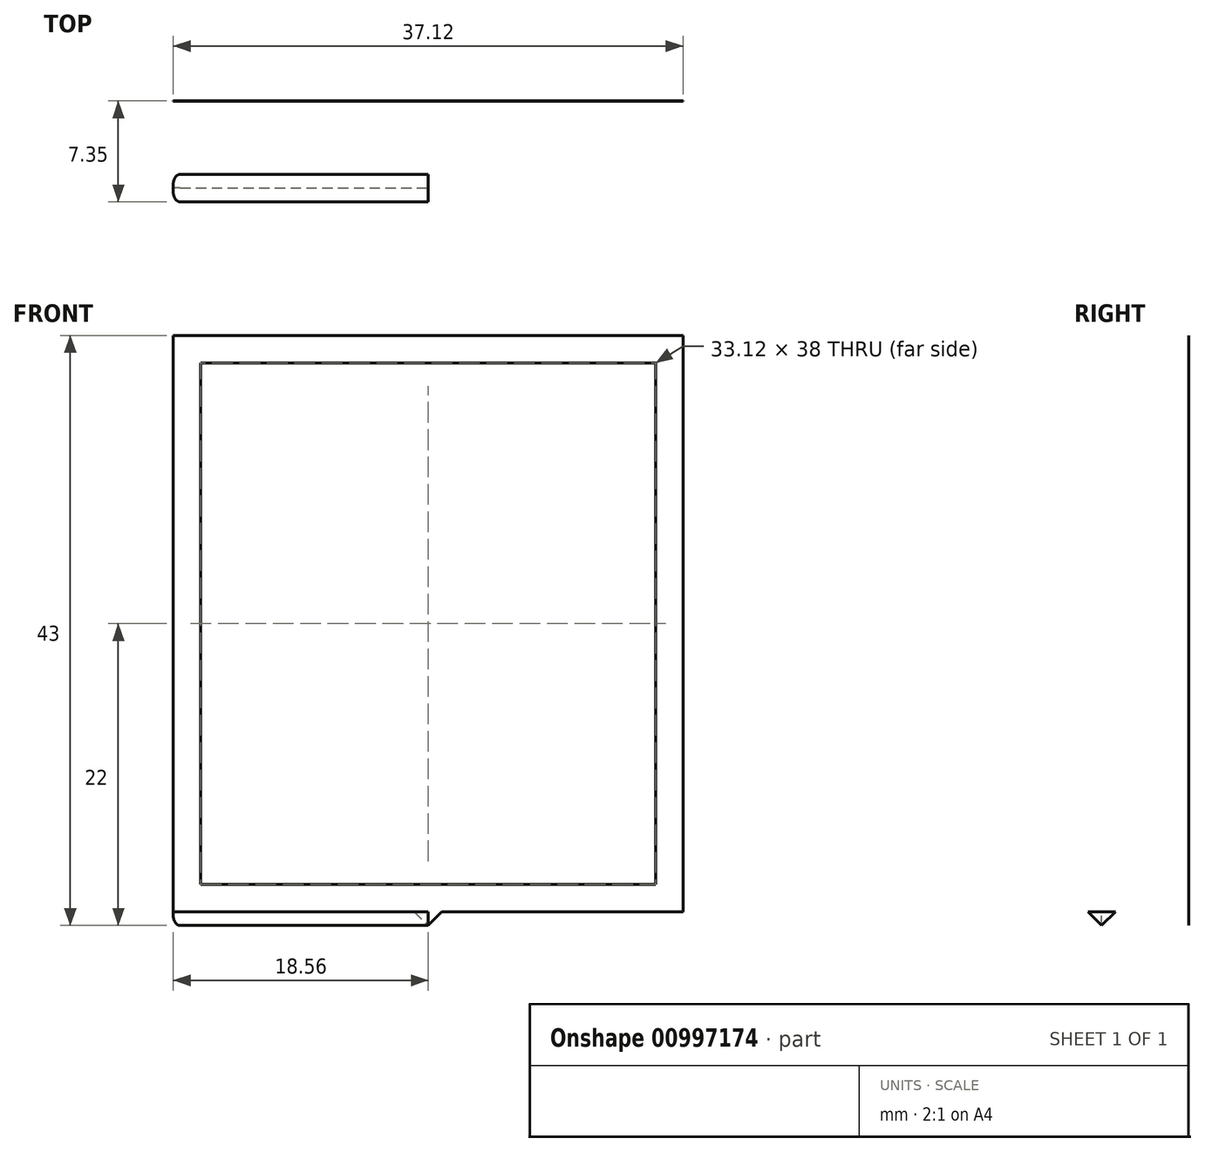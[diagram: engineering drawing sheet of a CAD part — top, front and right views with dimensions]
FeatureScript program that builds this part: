
annotation { "Feature Type Name" : "Feature", "Feature Type Description" : "" }
export const myFeature = defineFeature(function(context is Context, id is Id, definition is map)
    precondition{}
    {
        {
            var Q0;
            Q0=qCreatedBy(makeId("Front.planeOp"),FACE);
            var sketch = newSketch(context, id + "F0", { "sketchPlane" : qUnion([Q0])});
            skLineSegment(sketch, "E0", {"start": v(-24.91, 16.4) * mm, "end": v(-18.56, 16.4) * mm});
            skLineSegment(sketch, "E1", {"start": v(-18.56, 16.4) * mm, "end": v(-18.56, 0) * mm});
            skLineSegment(sketch, "E2", {"start": v(-18.56, 0) * mm, "end": v(0, 0) * mm});
            skLineSegment(sketch, "E3", {"start": v(0, 0) * mm, "end": v(0, 2) * mm});
            skLineSegment(sketch, "E4", {"start": v(0, 2) * mm, "end": v(-16.56, 2) * mm});
            skLineSegment(sketch, "E5", {"start": v(-16.56, 2) * mm, "end": v(-16.56, 40) * mm});
            skLineSegment(sketch, "E6", {"start": v(-16.56, 40) * mm, "end": v(0, 40) * mm});
            skLineSegment(sketch, "E7", {"start": v(0, 40) * mm, "end": v(0, 42) * mm});
            skLineSegment(sketch, "E8", {"start": v(0, 42) * mm, "end": v(-18.56, 42) * mm});
            skLineSegment(sketch, "E9", {"start": v(-18.56, 42) * mm, "end": v(-18.56, 18.4) * mm});
            skLineSegment(sketch, "E10", {"start": v(-18.56, 18.4) * mm, "end": v(-24.91, 18.4) * mm});
            skLineSegment(sketch, "E11", {"start": v(-24.91, 18.4) * mm, "end": v(-24.91, 16.4) * mm});
            skLineSegment(sketch, "E12", {"start": v(-16.56, 2) * mm, "end": v(-18.56, 2) * mm, "construction": true});
            skSolve(sketch);
        }
        {
            var Q0;
            Q0=qSketchRegion(id+"F0",true);
            extrude(context, id + "F1", {"entities" : qUnion([Q0]), "depth" : 1 / 50.8 * mm, "offsetDistance" : 25 * mm});
        }
        {
            var Q0;
            Q0=qCreatedBy(makeId("Front.planeOp"),FACE);
            var sketch = newSketch(context, id + "F2", { "sketchPlane" : qUnion([Q0])});
            skPoint(sketch, "E13.0", {"position": v(-18.56, 18.4) * mm});
            skPoint(sketch, "E14.0", {"position": v(-24.91, 16.4) * mm});
            skLineSegment(sketch, "E15.bottom", {"start": v(-24.91, 16.4) * mm, "end": v(-18.56, 16.4) * mm});
            skLineSegment(sketch, "E15.top", {"start": v(-24.91, 18.4) * mm, "end": v(-18.56, 18.4) * mm});
            skLineSegment(sketch, "E15.left", {"start": v(-24.91, 16.4) * mm, "end": v(-24.91, 18.4) * mm});
            skLineSegment(sketch, "E15.right", {"start": v(-18.56, 16.4) * mm, "end": v(-18.56, 18.4) * mm});
            skSolve(sketch);
        }
        {
            var Q0;
            Q0=qSketchRegion(id+"F2",true);
            extrude(context, id + "F3", {"entities" : qUnion([Q0]), "operationType" : NewBodyOperationType.REMOVE, "depth" : 25 * mm, "offsetDistance" : 25 * mm});
        }
        {
            var Q0;
            Q0=makeQuery(id+"FlJoKYSt8OexyGq_1.boolean.opBoolean","MERGE",FACE,{"derivedFrom":[makeQuery(id+"F1.opExtrude","SWEPT_FACE",FACE,{"disambiguationData":[OSD([sQuery(id+"F0.wireOp",EDGE,"E3")])]}),makeQuery(id+"FlJoKYSt8OexyGq_1.opExtrude","SWEPT_FACE",FACE,{"disambiguationData":[OSD([sQuery(id+"FTgjrMQJr4GTSXr_1.wireOp",EDGE,"iIzk7QKK-2KnJ-uT3C-CxSF-DB9qCKoUd3UN.right")])]})]});
            var sketch = newSketch(context, id + "F4", { "sketchPlane" : qUnion([Q0])});
            skPoint(sketch, "E16", {"position": v(-6.35, 2) * mm});
            skLineSegment(sketch, "E17", {"start": v(-6.35, 0) * mm, "end": v(-6.35, -1) * mm, "construction": true});
            skArc(sketch, "E18", {"start": v(-7.35, 0) * mm, "mid": v(-6.35, -1) * mm, "end": v(-5.35, 0) * mm, "construction": true});
            skLineSegment(sketch, "E19", {"start": v(-5.35, 0) * mm, "end": v(-7.35, 0) * mm});
            skLineSegment(sketch, "E20", {"start": v(-5.35, 0) * mm, "end": v(-6.35, -1) * mm});
            skLineSegment(sketch, "E21", {"start": v(-7.35, 0) * mm, "end": v(-6.35, -1) * mm});
            skSolve(sketch);
        }
        {
            var Q0;
            Q0=qSketchRegion(id+"F4",true);
            var Q1;
            Q1=makeQuery(id+"F1.opExtrude","CAP_VERTEX",VERTEX,{"disambiguationData":[OSD([sQuery(id+"F0.wireOp",EDGE,"E1"),sQuery(id+"F0.wireOp",EDGE,"E2")])],"isStart":true});
            extrude(context, id + "F5", {"entities" : qUnion([Q0]), "operationType" : NewBodyOperationType.ADD, "endBound" : BoundingType.UP_TO_VERTEX, "oppositeDirection" : true, "depth" : 25 * mm, "endBoundEntityVertex" : qUnion([Q1]), "offsetDistance" : 25 * mm});
        }
        {
            var Q0;
            Q0=makeQuery(id+"F1.opExtrude","SWEPT_BODY",BODY,{"disambiguationData":[OSD([sQuery(id+"F0.wireOp",EDGE,"E0"),sQuery(id+"F0.wireOp",EDGE,"E1"),sQuery(id+"F0.wireOp",EDGE,"E2"),sQuery(id+"F0.wireOp",EDGE,"E3"),sQuery(id+"F0.wireOp",EDGE,"E4"),sQuery(id+"F0.wireOp",EDGE,"E5"),sQuery(id+"F0.wireOp",EDGE,"E6"),sQuery(id+"F0.wireOp",EDGE,"E7"),sQuery(id+"F0.wireOp",EDGE,"E8"),sQuery(id+"F0.wireOp",EDGE,"E9"),sQuery(id+"F0.wireOp",EDGE,"E10"),sQuery(id+"F0.wireOp",EDGE,"E11")])]});
            var Q1;
            Q1=qCreatedBy(makeId("Right.planeOp"),FACE);
            mirror(context, id + "F6", {"operationType" : NewBodyOperationType.ADD, "entities" : qUnion([Q0]), "mirrorPlane" : qUnion([Q1])});
        }
        {
            var Q0;
            {var subQ0=makeQuery(id+"F1.opExtrude","SWEPT_FACE",FACE,{"disambiguationData":[OSD([sQuery(id+"F0.wireOp",EDGE,"E8")])]});Q0=makeQuery(id+"F6.boolean.opBoolean","MERGE",FACE,{"derivedFrom":[subQ0,makeQuery(id+"F6.opPattern","COPY",FACE,{"derivedFrom":subQ0,"instanceName":"1"})]});}
            var sketch = newSketch(context, id + "F7", { "sketchPlane" : qUnion([Q0])});
            skPoint(sketch, "E22", {"position": v(-11.56, -6.35) * mm});
            skPoint(sketch, "E22.positionSnap0", {"position": v(-18.56, -6.35) * mm});
            skPoint(sketch, "E23", {"position": v(0, -6.35) * mm});
            skPoint(sketch, "E24", {"position": v(11.56, -6.35) * mm});
            skLineSegment(sketch, "E25", {"start": v(11.56, -6.35) * mm, "end": v(0, -6.35) * mm, "construction": true});
            skLineSegment(sketch, "E26", {"start": v(0, -6.35) * mm, "end": v(-11.56, -6.35) * mm, "construction": true});
            skSolve(sketch);
        }
        {
            var Q0;
            {var subQ0=makeQuery(id+"F1.opExtrude","CAP_FACE",FACE,{"disambiguationData":[OSD([sQuery(id+"F0.wireOp",EDGE,"E0"),sQuery(id+"F0.wireOp",EDGE,"E1"),sQuery(id+"F0.wireOp",EDGE,"E2"),sQuery(id+"F0.wireOp",EDGE,"E3"),sQuery(id+"F0.wireOp",EDGE,"E4"),sQuery(id+"F0.wireOp",EDGE,"E5"),sQuery(id+"F0.wireOp",EDGE,"E6"),sQuery(id+"F0.wireOp",EDGE,"E7"),sQuery(id+"F0.wireOp",EDGE,"E8"),sQuery(id+"F0.wireOp",EDGE,"E9"),sQuery(id+"F0.wireOp",EDGE,"E10"),sQuery(id+"F0.wireOp",EDGE,"E11")])],"isStart":true});Q0=makeQuery(id+"F6.boolean.opBoolean","MERGE",FACE,{"derivedFrom":[subQ0,makeQuery(id+"F6.opPattern","COPY",FACE,{"derivedFrom":subQ0,"instanceName":"1"})]});}
            var sketch = newSketch(context, id + "F8", { "sketchPlane" : qUnion([Q0])});
            skArc(sketch, "E27", {"start": v(-1, 0) * mm, "mid": v(0, -1) * mm, "end": v(1, 0) * mm, "construction": true});
            skLineSegment(sketch, "E28", {"start": v(-1, 0) * mm, "end": v(1, 0) * mm});
            skLineSegment(sketch, "E29", {"start": v(1, 0) * mm, "end": v(0, -1) * mm});
            skLineSegment(sketch, "E30", {"start": v(0, -1) * mm, "end": v(-1, 0) * mm});
            skSolve(sketch);
        }
        {
            var Q0;
            Q0=qSketchRegion(id+"F8",true);
            var Q1;
            {var subQ0=makeQuery(id+"F1.opExtrude","CAP_FACE",FACE,{"disambiguationData":[OSD([sQuery(id+"F0.wireOp",EDGE,"E0"),sQuery(id+"F0.wireOp",EDGE,"E1"),sQuery(id+"F0.wireOp",EDGE,"E2"),sQuery(id+"F0.wireOp",EDGE,"E3"),sQuery(id+"F0.wireOp",EDGE,"E4"),sQuery(id+"F0.wireOp",EDGE,"E5"),sQuery(id+"F0.wireOp",EDGE,"E6"),sQuery(id+"F0.wireOp",EDGE,"E7"),sQuery(id+"F0.wireOp",EDGE,"E8"),sQuery(id+"F0.wireOp",EDGE,"E9"),sQuery(id+"F0.wireOp",EDGE,"E10"),sQuery(id+"F0.wireOp",EDGE,"E11")])],"isStart":false});Q1=makeQuery(id+"F6.boolean.opBoolean","MERGE",FACE,{"derivedFrom":[subQ0,makeQuery(id+"F6.opPattern","COPY",FACE,{"derivedFrom":subQ0,"instanceName":"1"})]});}
            extrude(context, id + "F9", {"entities" : qUnion([Q0]), "operationType" : NewBodyOperationType.ADD, "endBound" : BoundingType.UP_TO_SURFACE, "oppositeDirection" : true, "depth" : 25 * mm, "endBoundEntityFace" : qUnion([Q1]), "offsetDistance" : 25 * mm});
        }
        {
            var Q0;
            Q0=sQuery(id+"F7.wireOp",VERTEX,"E22");
            var Q1;
            Q1=sQuery(id+"F7.wireOp",VERTEX,"E23");
            var Q2;
            Q2=sQuery(id+"F7.wireOp",VERTEX,"E24");
            var Q3;
            Q3=makeQuery(id+"F1.opExtrude","SWEPT_BODY",BODY,{"disambiguationData":[OSD([sQuery(id+"F0.wireOp",EDGE,"E0"),sQuery(id+"F0.wireOp",EDGE,"E1"),sQuery(id+"F0.wireOp",EDGE,"E2"),sQuery(id+"F0.wireOp",EDGE,"E3"),sQuery(id+"F0.wireOp",EDGE,"E4"),sQuery(id+"F0.wireOp",EDGE,"E5"),sQuery(id+"F0.wireOp",EDGE,"E6"),sQuery(id+"F0.wireOp",EDGE,"E7"),sQuery(id+"F0.wireOp",EDGE,"E8"),sQuery(id+"F0.wireOp",EDGE,"E9"),sQuery(id+"F0.wireOp",EDGE,"E10"),sQuery(id+"F0.wireOp",EDGE,"E11")])]});
            hole(context, id + "F10", {"style" : HoleStyle.C_BORE, "endStyle" : HoleEndStyle.THROUGH, "holeDiameter" : 1 * mm, "cBoreDiameter" : 2 * mm, "cBoreDepth" : 41 * mm, "majorDiameter" : 5 * mm, "isTappedThrough" : true, "tappedDepth" : 12 * mm, "tapClearance" : 3, "startFromSketch" : true, "locations" : qUnion([Q0, Q1, Q2]), "scope" : qUnion([Q3])});
        }
        {
            var Q0;
            Q0=makeQuery(id+"F6.opPattern","COPY",EDGE,{"derivedFrom":makeQuery(id+"F3.boolean.opBoolean","INTERSECT",EDGE,{"derivedFrom":[makeQuery(id+"F1.opExtrude","CAP_FACE",FACE,{"disambiguationData":[OSD([sQuery(id+"F0.wireOp",EDGE,"E0"),sQuery(id+"F0.wireOp",EDGE,"E1"),sQuery(id+"F0.wireOp",EDGE,"E2"),sQuery(id+"F0.wireOp",EDGE,"E3"),sQuery(id+"F0.wireOp",EDGE,"E4"),sQuery(id+"F0.wireOp",EDGE,"E5"),sQuery(id+"F0.wireOp",EDGE,"E6"),sQuery(id+"F0.wireOp",EDGE,"E7"),sQuery(id+"F0.wireOp",EDGE,"E8"),sQuery(id+"F0.wireOp",EDGE,"E9"),sQuery(id+"F0.wireOp",EDGE,"E10"),sQuery(id+"F0.wireOp",EDGE,"E11")])],"isStart":false}),makeQuery(id+"F3.opExtrude","SWEPT_FACE",FACE,{"disambiguationData":[OSD([sQuery(id+"F2.wireOp",EDGE,"E15.right")])]})]}),"instanceName":"1"});
            var Q1;
            Q1=makeQuery(id+"F6.opPattern","COPY",EDGE,{"derivedFrom":makeQuery(id+"F1.opExtrude","CAP_EDGE",EDGE,{"disambiguationData":[OSD([sQuery(id+"F0.wireOp",EDGE,"E5")])],"isStart":false}),"instanceName":"1"});
            var Q2;
            {var subQ0=makeQuery(id+"F1.opExtrude","CAP_EDGE",EDGE,{"disambiguationData":[OSD([sQuery(id+"F0.wireOp",EDGE,"E8")])],"isStart":false});Q2=makeQuery(id+"F6.boolean.opBoolean","MERGE",EDGE,{"derivedFrom":[subQ0,makeQuery(id+"F6.opPattern","COPY",EDGE,{"derivedFrom":subQ0,"instanceName":"1"})]});}
            var Q3;
            {var subQ0=makeQuery(id+"F1.opExtrude","CAP_EDGE",EDGE,{"disambiguationData":[OSD([sQuery(id+"F0.wireOp",EDGE,"E6")])],"isStart":false});Q3=makeQuery(id+"F6.boolean.opBoolean","MERGE",EDGE,{"derivedFrom":[subQ0,makeQuery(id+"F6.opPattern","COPY",EDGE,{"derivedFrom":subQ0,"instanceName":"1"})]});}
            var Q4;
            Q4=makeQuery(id+"F1.opExtrude","CAP_EDGE",EDGE,{"disambiguationData":[OSD([sQuery(id+"F0.wireOp",EDGE,"E5")])],"isStart":false});
            var Q5;
            Q5=makeQuery(id+"F3.boolean.opBoolean","INTERSECT",EDGE,{"derivedFrom":[makeQuery(id+"F1.opExtrude","CAP_FACE",FACE,{"disambiguationData":[OSD([sQuery(id+"F0.wireOp",EDGE,"E0"),sQuery(id+"F0.wireOp",EDGE,"E1"),sQuery(id+"F0.wireOp",EDGE,"E2"),sQuery(id+"F0.wireOp",EDGE,"E3"),sQuery(id+"F0.wireOp",EDGE,"E4"),sQuery(id+"F0.wireOp",EDGE,"E5"),sQuery(id+"F0.wireOp",EDGE,"E6"),sQuery(id+"F0.wireOp",EDGE,"E7"),sQuery(id+"F0.wireOp",EDGE,"E8"),sQuery(id+"F0.wireOp",EDGE,"E9"),sQuery(id+"F0.wireOp",EDGE,"E10"),sQuery(id+"F0.wireOp",EDGE,"E11")])],"isStart":false}),makeQuery(id+"F3.opExtrude","SWEPT_FACE",FACE,{"disambiguationData":[OSD([sQuery(id+"F2.wireOp",EDGE,"E15.right")])]})]});
            var Q6;
            Q6=makeQuery(id+"F6.opPattern","COPY",EDGE,{"derivedFrom":makeQuery(id+"F1.opExtrude","SWEPT_EDGE",EDGE,{"disambiguationData":[OSD([sQuery(id+"F0.wireOp",EDGE,"E8"),sQuery(id+"F0.wireOp",EDGE,"E9")])]}),"instanceName":"1"});
            var Q7;
            Q7=makeQuery(id+"F1.opExtrude","SWEPT_EDGE",EDGE,{"disambiguationData":[OSD([sQuery(id+"F0.wireOp",EDGE,"E8"),sQuery(id+"F0.wireOp",EDGE,"E9")])]});
            var Q8;
            Q8=makeQuery(id+"F6.opPattern","COPY",EDGE,{"derivedFrom":makeQuery(id+"F3.boolean.opBoolean","MERGE",EDGE,{"derivedFrom":[makeQuery(id+"F1.opExtrude","CAP_EDGE",EDGE,{"disambiguationData":[OSD([sQuery(id+"F0.wireOp",EDGE,"E1")])],"isStart":true}),makeQuery(id+"F1.opExtrude","CAP_EDGE",EDGE,{"disambiguationData":[OSD([sQuery(id+"F0.wireOp",EDGE,"E9")])],"isStart":true})],"fromTools":[makeQuery(id+"F3.opExtrude","CAP_EDGE",EDGE,{"disambiguationData":[OSD([sQuery(id+"F2.wireOp",EDGE,"E15.right")])],"isStart":true})]}),"instanceName":"1"});
            var Q9;
            {var subQ0=makeQuery(id+"F1.opExtrude","CAP_EDGE",EDGE,{"disambiguationData":[OSD([sQuery(id+"F0.wireOp",EDGE,"E8")])],"isStart":true});Q9=makeQuery(id+"F6.boolean.opBoolean","MERGE",EDGE,{"derivedFrom":[subQ0,makeQuery(id+"F6.opPattern","COPY",EDGE,{"derivedFrom":subQ0,"instanceName":"1"})]});}
            var Q10;
            Q10=makeQuery(id+"F3.boolean.opBoolean","MERGE",EDGE,{"derivedFrom":[makeQuery(id+"F1.opExtrude","CAP_EDGE",EDGE,{"disambiguationData":[OSD([sQuery(id+"F0.wireOp",EDGE,"E1")])],"isStart":true}),makeQuery(id+"F1.opExtrude","CAP_EDGE",EDGE,{"disambiguationData":[OSD([sQuery(id+"F0.wireOp",EDGE,"E9")])],"isStart":true})],"fromTools":[makeQuery(id+"F3.opExtrude","CAP_EDGE",EDGE,{"disambiguationData":[OSD([sQuery(id+"F2.wireOp",EDGE,"E15.right")])],"isStart":true})]});
            var Q11;
            {var subQ0=makeQuery(id+"F1.opExtrude","CAP_EDGE",EDGE,{"disambiguationData":[OSD([sQuery(id+"F0.wireOp",EDGE,"E6")])],"isStart":true});Q11=makeQuery(id+"F6.boolean.opBoolean","MERGE",EDGE,{"derivedFrom":[subQ0,makeQuery(id+"F6.opPattern","COPY",EDGE,{"derivedFrom":subQ0,"instanceName":"1"})]});}
            var Q12;
            Q12=makeQuery(id+"F6.opPattern","COPY",EDGE,{"derivedFrom":makeQuery(id+"F1.opExtrude","CAP_EDGE",EDGE,{"disambiguationData":[OSD([sQuery(id+"F0.wireOp",EDGE,"E5")])],"isStart":true}),"instanceName":"1"});
            var Q13;
            Q13=makeQuery(id+"F1.opExtrude","CAP_EDGE",EDGE,{"disambiguationData":[OSD([sQuery(id+"F0.wireOp",EDGE,"E5")])],"isStart":true});
            var Q14;
            {var subQ0=makeQuery(id+"F1.opExtrude","CAP_EDGE",EDGE,{"disambiguationData":[OSD([sQuery(id+"F0.wireOp",EDGE,"E4")])],"isStart":true});Q14=makeQuery(id+"F6.boolean.opBoolean","MERGE",EDGE,{"derivedFrom":[subQ0,makeQuery(id+"F6.opPattern","COPY",EDGE,{"derivedFrom":subQ0,"instanceName":"1"})]});}
            var Q15;
            {var subQ0=sQuery(id+"F0.wireOp",EDGE,"E2");var subQ2=sQuery(id+"F0.wireOp",EDGE,"E1");var subQ3=makeQuery(id+"F1.opExtrude","SWEPT_FACE",FACE,{"disambiguationData":[OSD([subQ2])]});var subQ13=makeQuery(id+"F1.opExtrude","CAP_EDGE",EDGE,{"disambiguationData":[OSD([subQ0])],"isStart":true});Q15=makeQuery(id+"F9.boolean.opBoolean","SPLIT",EDGE,{"disambiguationData":[TD([subQ3])],"derivedFrom":makeQuery(id+"F6.boolean.opBoolean","MERGE",EDGE,{"derivedFrom":[subQ13,makeQuery(id+"F6.opPattern","COPY",EDGE,{"derivedFrom":subQ13,"instanceName":"1"})]})});}
            var Q16;
            {var subQ0=sQuery(id+"F0.wireOp",EDGE,"E2");var subQ12=sQuery(id+"F8.wireOp",EDGE,"E30");var subQ13=makeQuery(id+"F1.opExtrude","CAP_EDGE",EDGE,{"disambiguationData":[OSD([subQ0])],"isStart":true});Q16=makeQuery(id+"F9.boolean.opBoolean","SPLIT",EDGE,{"disambiguationData":[TD([makeQuery(id+"F9.opExtrude","SWEPT_FACE",FACE,{"disambiguationData":[OSD([subQ12])]})])],"derivedFrom":makeQuery(id+"F6.boolean.opBoolean","MERGE",EDGE,{"derivedFrom":[subQ13,makeQuery(id+"F6.opPattern","COPY",EDGE,{"derivedFrom":subQ13,"instanceName":"1"})]})});}
            var Q17;
            {var subQ2=sQuery(id+"F0.wireOp",EDGE,"E2");var subQ5=sQuery(id+"F0.wireOp",EDGE,"E1");var subQ6=makeQuery(id+"F1.opExtrude","SWEPT_FACE",FACE,{"disambiguationData":[OSD([subQ5])]});var subQ13=makeQuery(id+"F1.opExtrude","CAP_EDGE",EDGE,{"disambiguationData":[OSD([subQ2])],"isStart":false});Q17=makeQuery(id+"F9.boolean.opBoolean","SPLIT",EDGE,{"disambiguationData":[TD([subQ6])],"derivedFrom":makeQuery(id+"F6.boolean.opBoolean","MERGE",EDGE,{"derivedFrom":[subQ13,makeQuery(id+"F6.opPattern","COPY",EDGE,{"derivedFrom":subQ13,"instanceName":"1"})]})});}
            var Q18;
            {var subQ8=sQuery(id+"F0.wireOp",EDGE,"E2");var subQ10=sQuery(id+"F8.wireOp",EDGE,"E30");var subQ13=makeQuery(id+"F1.opExtrude","CAP_EDGE",EDGE,{"disambiguationData":[OSD([subQ8])],"isStart":false});Q18=makeQuery(id+"F9.boolean.opBoolean","SPLIT",EDGE,{"disambiguationData":[TD([makeQuery(id+"F9.opExtrude","SWEPT_FACE",FACE,{"disambiguationData":[OSD([subQ10])]})])],"derivedFrom":makeQuery(id+"F6.boolean.opBoolean","MERGE",EDGE,{"derivedFrom":[subQ13,makeQuery(id+"F6.opPattern","COPY",EDGE,{"derivedFrom":subQ13,"instanceName":"1"})]})});}
            var Q19;
            {var subQ0=makeQuery(id+"F1.opExtrude","CAP_EDGE",EDGE,{"disambiguationData":[OSD([sQuery(id+"F0.wireOp",EDGE,"E4")])],"isStart":false});Q19=makeQuery(id+"F6.boolean.opBoolean","MERGE",EDGE,{"derivedFrom":[subQ0,makeQuery(id+"F6.opPattern","COPY",EDGE,{"derivedFrom":subQ0,"instanceName":"1"})]});}
            var Q20;
            {var subQ1=sQuery(id+"F0.wireOp",EDGE,"E2");var subQ2=sQuery(id+"F0.wireOp",EDGE,"E1");var subQ3=sQuery(id+"F4.wireOp",EDGE,"E21");Q20=makeQuery(id+"F6.opPattern","COPY",EDGE,{"derivedFrom":makeQuery(id+"F5.boolean.opBoolean","SPLIT",EDGE,{"disambiguationData":[TD([makeQuery(id+"F5.opExtrude","SWEPT_FACE",FACE,{"disambiguationData":[OSD([subQ3])]})])],"derivedFrom":makeQuery(id+"F1.opExtrude","SWEPT_EDGE",EDGE,{"disambiguationData":[OSD([subQ2,subQ1])]})}),"instanceName":"1"});}
            var Q21;
            {var subQ0=sQuery(id+"F0.wireOp",EDGE,"E2");var subQ1=sQuery(id+"F0.wireOp",EDGE,"E1");var subQ3=sQuery(id+"F4.wireOp",EDGE,"E20");Q21=makeQuery(id+"F6.opPattern","COPY",EDGE,{"derivedFrom":makeQuery(id+"F5.boolean.opBoolean","SPLIT",EDGE,{"disambiguationData":[TD([makeQuery(id+"F5.opExtrude","SWEPT_FACE",FACE,{"disambiguationData":[OSD([subQ3])]})])],"derivedFrom":makeQuery(id+"F1.opExtrude","SWEPT_EDGE",EDGE,{"disambiguationData":[OSD([subQ1,subQ0])]})}),"instanceName":"1"});}
            var Q22;
            {var subQ1=sQuery(id+"F0.wireOp",EDGE,"E2");var subQ2=sQuery(id+"F0.wireOp",EDGE,"E1");var subQ3=sQuery(id+"F4.wireOp",EDGE,"E21");Q22=makeQuery(id+"F5.boolean.opBoolean","SPLIT",EDGE,{"disambiguationData":[TD([makeQuery(id+"F5.opExtrude","SWEPT_FACE",FACE,{"disambiguationData":[OSD([subQ3])]})])],"derivedFrom":makeQuery(id+"F1.opExtrude","SWEPT_EDGE",EDGE,{"disambiguationData":[OSD([subQ2,subQ1])]})});}
            var Q23;
            {var subQ0=sQuery(id+"F0.wireOp",EDGE,"E2");var subQ1=sQuery(id+"F0.wireOp",EDGE,"E1");var subQ3=sQuery(id+"F4.wireOp",EDGE,"E20");Q23=makeQuery(id+"F5.boolean.opBoolean","SPLIT",EDGE,{"disambiguationData":[TD([makeQuery(id+"F5.opExtrude","SWEPT_FACE",FACE,{"disambiguationData":[OSD([subQ3])]})])],"derivedFrom":makeQuery(id+"F1.opExtrude","SWEPT_EDGE",EDGE,{"disambiguationData":[OSD([subQ1,subQ0])]})});}
            var Q24;
            Q24=makeQuery(id+"F5.opExtrude","CAP_EDGE",EDGE,{"disambiguationData":[OSD([sQuery(id+"F4.wireOp",EDGE,"E21")])],"isStart":false});
            var Q25;
            Q25=makeQuery(id+"F5.opExtrude","CAP_EDGE",EDGE,{"disambiguationData":[OSD([sQuery(id+"F4.wireOp",EDGE,"E20")])],"isStart":false});
            var Q26;
            Q26=makeQuery(id+"F6.opPattern","COPY",EDGE,{"derivedFrom":makeQuery(id+"F5.opExtrude","CAP_EDGE",EDGE,{"disambiguationData":[OSD([sQuery(id+"F4.wireOp",EDGE,"E21")])],"isStart":false}),"instanceName":"1"});
            var Q27;
            Q27=makeQuery(id+"F6.opPattern","COPY",EDGE,{"derivedFrom":makeQuery(id+"F5.opExtrude","CAP_EDGE",EDGE,{"disambiguationData":[OSD([sQuery(id+"F4.wireOp",EDGE,"E20")])],"isStart":false}),"instanceName":"1"});
            fillet(context, id + "F11", {"entities" : qUnion([Q0, Q1, Q2, Q3, Q4, Q5, Q6, Q7, Q8, Q9, Q10, Q11, Q12, Q13, Q14, Q15, Q16, Q17, Q18, Q19, Q20, Q21, Q22, Q23, Q24, Q25, Q26, Q27]), "radius" : .5 * mm, "tangentPropagation" : true, "allowEdgeOverflow" : false});
        }
    });
